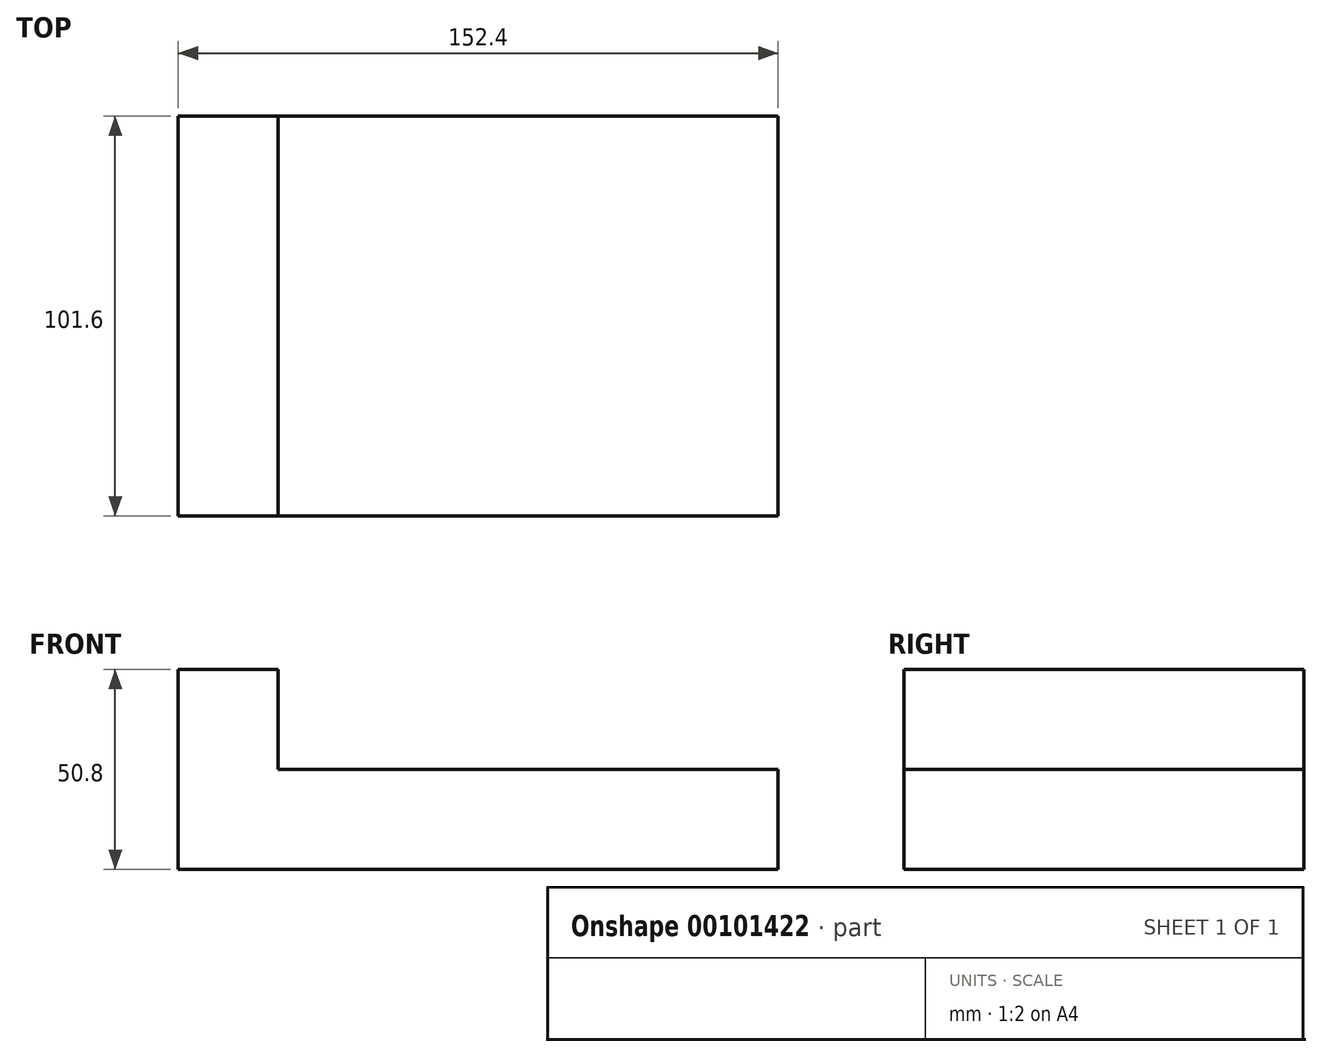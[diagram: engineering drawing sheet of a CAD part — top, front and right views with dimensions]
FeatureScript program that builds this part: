
annotation { "Feature Type Name" : "Feature", "Feature Type Description" : "" }
export const myFeature = defineFeature(function(context is Context, id is Id, definition is map)
    precondition{}
    {
        {
            var Q0;
            Q0=qCreatedBy(makeId("Top.planeOp"),FACE);
            var sketch = newSketch(context, id + "F0", { "sketchPlane" : qUnion([Q0])});
            skLineSegment(sketch, "E0", {"start": v(-109.14, 22.8) * mm, "end": v(-109.14, -78.8) * mm});
            skLineSegment(sketch, "E1", {"start": v(-109.14, -78.8) * mm, "end": v(17.86, -78.8) * mm});
            skLineSegment(sketch, "E2", {"start": v(17.86, -78.8) * mm, "end": v(17.86, 22.8) * mm});
            skLineSegment(sketch, "E3", {"start": v(17.86, 22.8) * mm, "end": v(-109.14, 22.8) * mm});
            skSolve(sketch);
        }
        {
            var Q0;
            Q0 = qSketchRegion(id + "F0", true);
            extrude(context, id + "F1", {"entities" : qUnion([Q0]), "depth" : 25.4 * mm});
        }
        {
            var Q0;
            Q0=makeQuery(id+"F1.opExtrude","SWEPT_FACE",FACE,{"disambiguationData":[OSD([sQuery(id+"F0.wireOp",EDGE,"E0")])]});
            var sketch = newSketch(context, id + "F2", { "sketchPlane" : qUnion([Q0])});
            skLineSegment(sketch, "E4", {"start": v(-22.8, 0) * mm, "end": v(-22.8, 50.8) * mm});
            skLineSegment(sketch, "E5", {"start": v(-22.8, 50.8) * mm, "end": v(78.8, 50.8) * mm});
            skLineSegment(sketch, "E6", {"start": v(78.8, 50.8) * mm, "end": v(78.8, 0) * mm});
            skLineSegment(sketch, "E7", {"start": v(78.8, 0) * mm, "end": v(-22.8, 0) * mm});
            skSolve(sketch);
        }
        {
            var Q0;
            Q0 = qSketchRegion(id + "F2", true);
            extrude(context, id + "F3", {"entities" : qUnion([Q0]), "operationType" : NewBodyOperationType.ADD, "depth" : 25.4 * mm});
        }
    });
